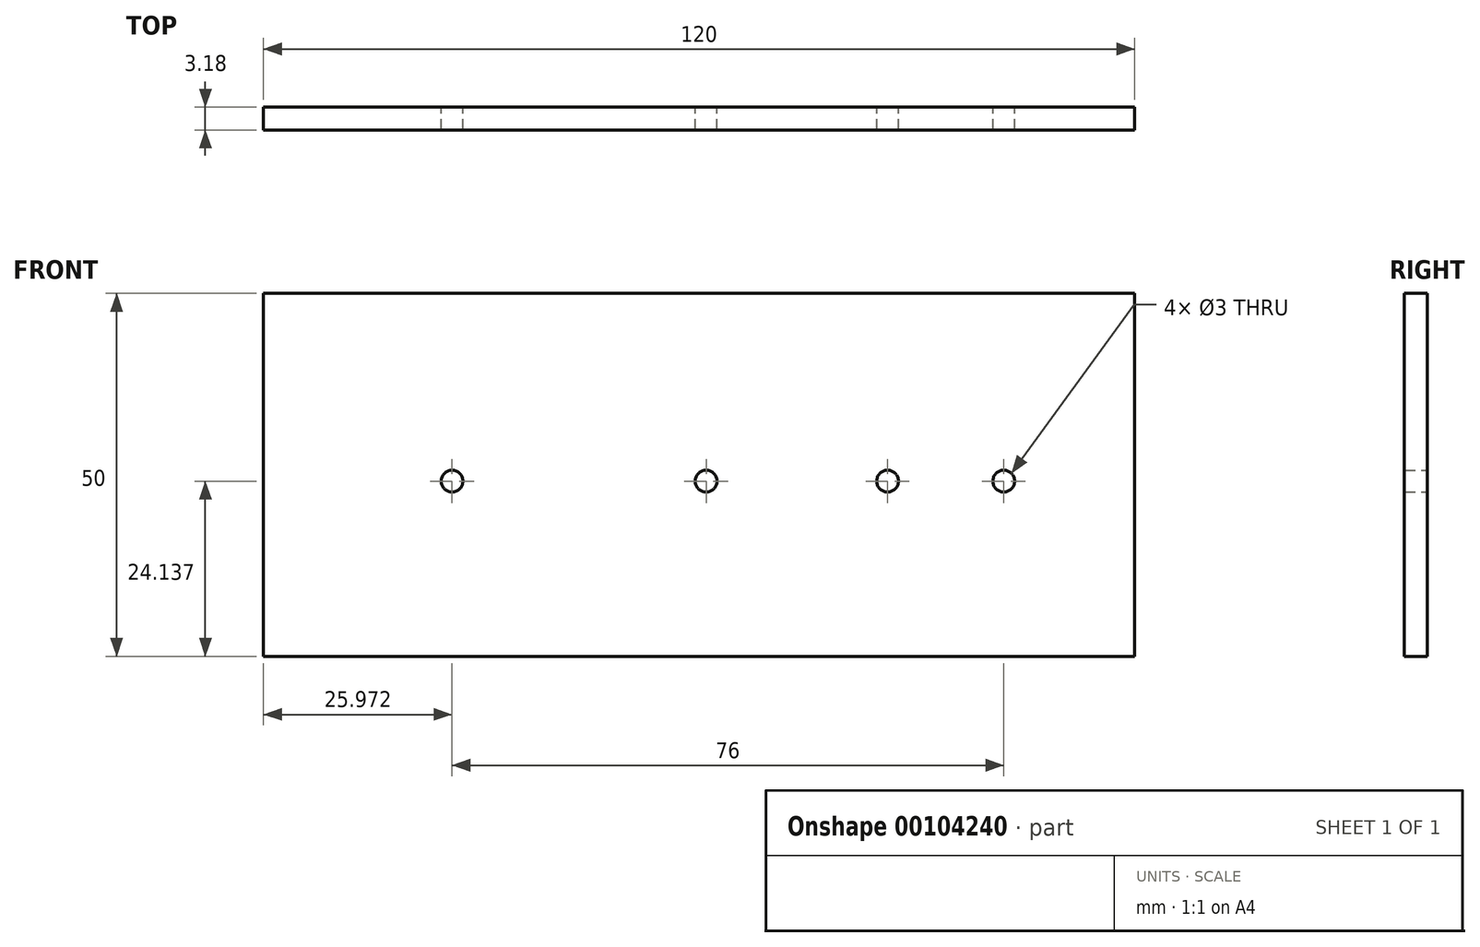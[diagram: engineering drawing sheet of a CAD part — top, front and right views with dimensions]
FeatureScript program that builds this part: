
annotation { "Feature Type Name" : "Feature", "Feature Type Description" : "" }
export const myFeature = defineFeature(function(context is Context, id is Id, definition is map)
    precondition{}
    {
        {
            var Q0;
            Q0=qCreatedBy(makeId("Front.planeOp"),FACE);
            var sketch = newSketch(context, id + "F0", { "sketchPlane" : qUnion([Q0])});
            skLineSegment(sketch, "E0.bottom", {"start": v(-119.64, 26.83) * mm, "end": v(0.36, 26.83) * mm});
            skLineSegment(sketch, "E0.top", {"start": v(-119.64, -23.17) * mm, "end": v(0.36, -23.17) * mm});
            skLineSegment(sketch, "E0.left", {"start": v(-119.64, 26.83) * mm, "end": v(-119.64, -23.17) * mm});
            skLineSegment(sketch, "E0.right", {"start": v(0.36, 26.83) * mm, "end": v(0.36, -23.17) * mm});
            skLineSegment(sketch, "E1", {"start": v(-93.67, 0.97) * mm, "end": v(-58.67, 0.97) * mm});
            skLineSegment(sketch, "E2", {"start": v(-58.67, 0.97) * mm, "end": v(-33.67, 0.97) * mm});
            skLineSegment(sketch, "E3", {"start": v(-33.67, 0.97) * mm, "end": v(-17.67, 0.97) * mm});
            skCircle(sketch, "E4", {"center": v(-93.67, 0.97) * mm, "radius": 1.5 * mm});
            skCircle(sketch, "E5", {"center": v(-58.67, 0.97) * mm, "radius": 1.5 * mm});
            skCircle(sketch, "E6", {"center": v(-33.67, 0.97) * mm, "radius": 1.5 * mm});
            skCircle(sketch, "E7", {"center": v(-17.67, 0.97) * mm, "radius": 1.5 * mm});
            skSolve(sketch);
        }
        {
            var Q0;
            Q0=makeQuery(id+"F0.imprint","IMPRINT",FACE,{"disambiguationData":[TD([[makeQuery(id+"F0.imprint","IMPRINT",EDGE,{"derivedFrom":sQuery(id+"F0.wireOp",EDGE,"E0.bottom")}),-1.0]])]});
            extrude(context, id + "F1", {"entities" : qUnion([Q0]), "depth" : 3.17 * mm});
        }
    });
